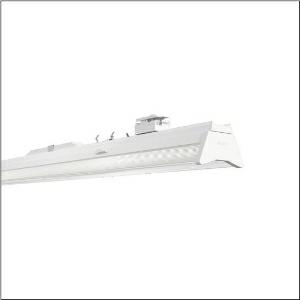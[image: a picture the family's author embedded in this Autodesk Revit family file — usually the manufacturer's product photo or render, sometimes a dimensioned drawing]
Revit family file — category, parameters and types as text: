
# Revit family: licross_r__11_performance_mo_51tm16cn49xg_d1b9
name_source: partatom
category: Lighting Fixtures
units: mm (PartAtom-declared; Revit-internal decimal feet)

## family parameters
Cut with Voids When Loaded = No
Host = Face
Light Source = No
Part Type = Normal
Room Calculation Point = No
Round Connector Dimension = Use Diameter
Shared = No

## types (1)
- --- (1 x LED, 9190 lm, 49.4 W, 4000K)
    Apparent Load = 49 VA
    CIE Flux Codes = 66 88 96 79 100
    Color Rendering = 80
    Color Temperature = 4000K
    Default Elevation = 1800 mm
    Description = Licross® 11 Performance MO, luminaire insert, of sheet steel, galvanised, coil coated, white, length: 1.500mm, width: 120mm, height: 123mm, LED rated luminous flux: 9.190lm, light colour: 840, control gear: ON/OFF Multilumen, CLOi, with plug, 3-pole, with phase selection, mains connection: 220..240V, AC, 50/60Hz, start of lifetime: 49W, end of service life: 55W, halogen-free wiring, primary light control with lens, of plastic, primary optical cover: cover, of PMMA, light emission: direct/indirect distribution, primary light characteristic: symmetric, protection rating (complete): IP40, insulation class (complete): insulation class I (protective earthing), certification: CE, ENEC, VDE, UKCA, protection symbol: D if used in an environment without relevant dust loads with corresponding accessories, impact resistance: IK06, permissible ambient temperature for indoor applications: -35..+40°C, corresponds to IFS (International Featured Standards) requirements for safety and quality in the food industry, reducing of maximum allowable ambient temperature of 5°C with ceiling mounting, LABS conformity tested according to VDMA 24364:2018-05, packaging unit: 1 piece
    Height = 114 mm
    Lamp = 1 x LED
    Lamp Light Flux = 9190 lm
    Lamp Power = 49.4 W
    Lamp count = 1
    Length = 1500 mm
    Luminous efficacy = 186 lm/W
    Manufacturer = Siteco
    ModVariant = No
    Model = 51TM16CN49XG
    Mounting Place = Ceiling
    Mounting Type = Pendant
    Number of Poles = 1
    OnlyDefault = Yes
    Power Factor = 1
    Product Name = Licross® 11 Performance MO
    Product group = luminaire insert
    ProductGroupID = 902
    Protection Class = Protection class I
    Protection Degree = IP 40
    RLX_Detail_Level = 1
    RLX_Emergency_Light_Flux = 0 lm
    RLX_Emergency_Type = 0
    RLX_Emergency_Type_DB = No
    RlxData = <blob elided: 31805 chars, md5=a745e388>
    Socket = socket
    Standby Power = 0 W
    System Light Flux = 9190 lm
    System Power = 49 W
    Type Comments = factory setting: luminous flux: 100 % | (A | C | E) | 113 mA
    Type Image = l_1256138.jpg
    URL = http://relux.com
    VarID = @adj_086086
    Voltage = 0 V
    Weight = 0.00 kg
    Width = 120 mm

## geometry (parser evidence)
native form markers: Blend x4, Sweep x12
no freeform markers — native parametric forms only
